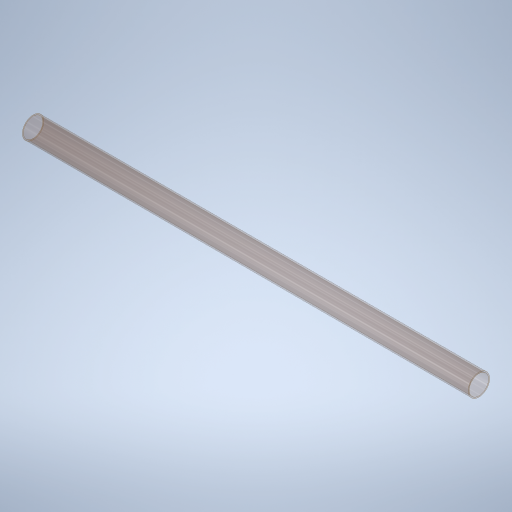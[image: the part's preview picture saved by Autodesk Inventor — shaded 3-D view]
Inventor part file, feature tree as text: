
AUTODESK INVENTOR PART (.ipt)
format: ipt  version: 2023.4 (Build 274418000, 418)  size: 264,704 bytes
history: native  units: in
note: dims shown in document units (in); Inventor stores cm internally (conversion verified against a paired STEP export)
features: extrude x1, sketch x1
ambient origin geometry x8: Origin, YZ Plane, XZ Plane, XY Plane, X Axis, Y Axis, Z Axis, Center Point
bodies: Solid1 (feature_tree)
feature tree (2):
  extrude  "Extrusion1"  Depth=25.875in
  sketch  "Sketch1"  dims[d0=1.25in d2=0.0625in d3=25.875in d4=0.0in]
